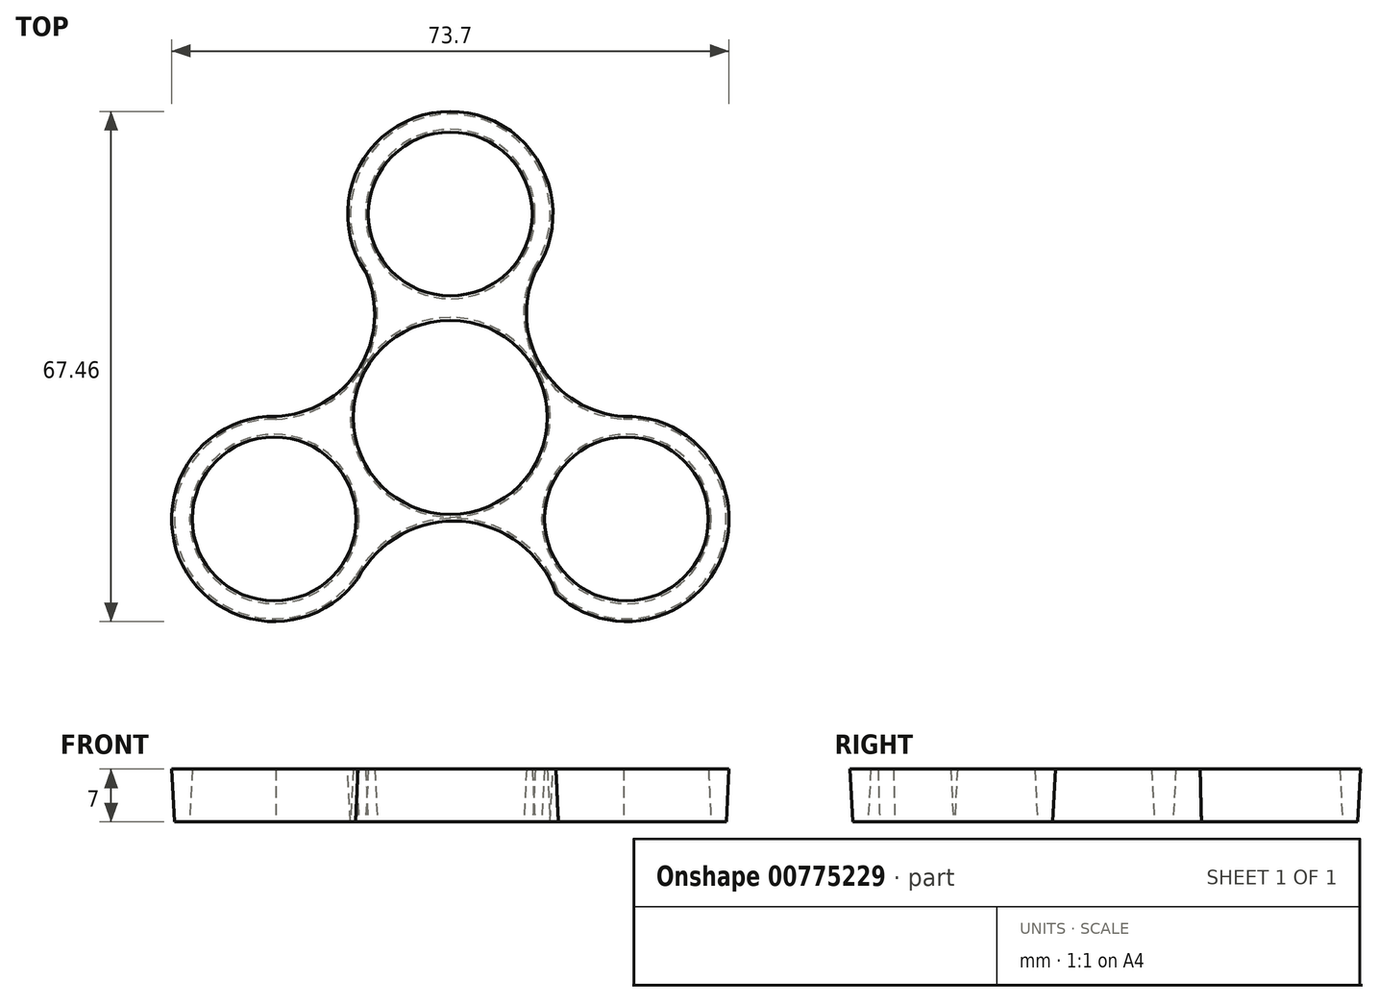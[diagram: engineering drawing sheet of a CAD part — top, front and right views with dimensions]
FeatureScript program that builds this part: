
annotation { "Feature Type Name" : "Feature", "Feature Type Description" : "" }
export const myFeature = defineFeature(function(context is Context, id is Id, definition is map)
    precondition{}
    {
        {
            var Q0;
            Q0=qCreatedBy(makeId("Top.planeOp"),FACE);
            var sketch = newSketch(context, id + "F0", { "sketchPlane" : qUnion([Q0])});
            skCircle(sketch, "E0", {"center": v(0, 0) * mm, "radius": 11.2 * mm});
            skCircle(sketch, "E1", {"center": v(0, 0) * mm, "radius": 13.2 * mm});
            skCircle(sketch, "E2", {"center": v(0, 26.88) * mm, "radius": 11.2 * mm});
            skCircle(sketch, "E3", {"center": v(0, 26.88) * mm, "radius": 13.2 * mm});
            skCircle(sketch, "E4.1.0", {"center": v(-23.28, -13.44) * mm, "radius": 13.2 * mm});
            skCircle(sketch, "E4.1.1", {"center": v(-23.28, -13.44) * mm, "radius": 11.2 * mm});
            skCircle(sketch, "E4.2.0", {"center": v(23.28, -13.44) * mm, "radius": 13.2 * mm});
            skCircle(sketch, "E4.2.1", {"center": v(23.28, -13.44) * mm, "radius": 11.2 * mm});
            skArc(sketch, "E5", {"start": v(10.9, 19.44) * mm, "mid": v(11.76, 6.46) * mm, "end": v(22.9, -0.25) * mm});
            skArc(sketch, "E6", {"start": v(14.28, -23.1) * mm, "mid": v(1.54, -13.4) * mm, "end": v(-12.52, -21.08) * mm});
            skArc(sketch, "E7", {"start": v(-23.05, -0.24) * mm, "mid": v(-11.71, 6.33) * mm, "end": v(-10.88, 19.4) * mm});
            skSolve(sketch);
        }
        {
            var Q0;
            Q0=makeQuery(id+"F0.imprint","IMPRINT",FACE,{"disambiguationData":[TD([[makeQuery(id+"F0.imprint","IMPRINT",EDGE,{"derivedFrom":sQuery(id+"F0.wireOp",EDGE,"E1")}),-1.0]])]});
            var Q1;
            Q1=makeQuery(id+"F0.imprint","IMPRINT",FACE,{"disambiguationData":[TD([[makeQuery(id+"F0.imprint","IMPRINT",EDGE,{"derivedFrom":sQuery(id+"F0.wireOp",EDGE,"E4.2.1")}),-1.0]])]});
            var Q2;
            Q2=makeQuery(id+"F0.imprint","IMPRINT",FACE,{"disambiguationData":[TD([[makeQuery(id+"F0.imprint","IMPRINT",EDGE,{"derivedFrom":sQuery(id+"F0.wireOp",EDGE,"E2")}),-1.0]])]});
            var Q3;
            Q3=makeQuery(id+"F0.imprint","IMPRINT",FACE,{"disambiguationData":[TD([[makeQuery(id+"F0.imprint","IMPRINT",EDGE,{"derivedFrom":sQuery(id+"F0.wireOp",EDGE,"E4.1.1")}),-1.0]])]});
            extrude(context, id + "F1", {"entities" : qUnion([Q0, Q1, Q2, Q3]), "depth" : 7 * mm, "offsetDistance" : 25 * mm, "hasDraft" : true, "draftAngle" : 3 * degree});
        }
    });
